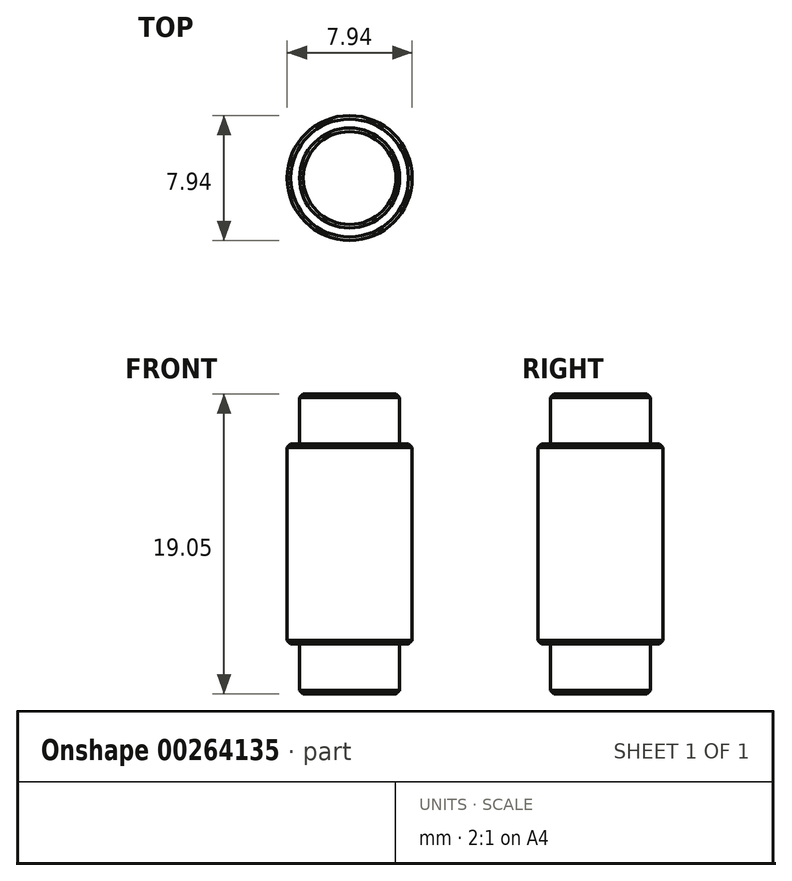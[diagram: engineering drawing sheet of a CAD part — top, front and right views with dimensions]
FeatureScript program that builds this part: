
annotation { "Feature Type Name" : "Feature", "Feature Type Description" : "" }
export const myFeature = defineFeature(function(context is Context, id is Id, definition is map)
    precondition{}
    {
        {
            var Q0;
            Q0=qCreatedBy(makeId("Top.planeOp"),FACE);
            var sketch = newSketch(context, id + "F0", { "sketchPlane" : qUnion([Q0])});
            skCircle(sketch, "E0", {"center": v(0, 0) * mm, "radius": 3.18 * mm});
            skSolve(sketch);
        }
        {
            var Q0;
            Q0 = qSketchRegion(id + "F0", true);
            extrude(context, id + "F1", {"entities" : qUnion([Q0]), "depth" : 3.17 * mm});
        }
        {
            var Q0;
            Q0=makeQuery(id+"F1.opExtrude","CAP_FACE",FACE,{"disambiguationData":[OSD([sQuery(id+"F0.wireOp",EDGE,"E0")])],"isStart":false});
            var sketch = newSketch(context, id + "F2", { "sketchPlane" : qUnion([Q0])});
            skCircle(sketch, "E1", {"center": v(0, 0) * mm, "radius": 3.97 * mm});
            skSolve(sketch);
        }
        {
            var Q0;
            Q0 = qSketchRegion(id + "F2", true);
            extrude(context, id + "F3", {"entities" : qUnion([Q0]), "operationType" : NewBodyOperationType.ADD, "depth" : 12.7 * mm});
        }
        {
            var Q0;
            Q0=makeQuery(id+"F3.opExtrude","CAP_FACE",FACE,{"disambiguationData":[OSD([sQuery(id+"F2.wireOp",EDGE,"E1")])],"isStart":false});
            var sketch = newSketch(context, id + "F4", { "sketchPlane" : qUnion([Q0])});
            skCircle(sketch, "E2", {"center": v(0, 0) * mm, "radius": 3.18 * mm});
            skSolve(sketch);
        }
        {
            var Q0;
            Q0 = qSketchRegion(id + "F4", true);
            extrude(context, id + "F5", {"entities" : qUnion([Q0]), "operationType" : NewBodyOperationType.ADD, "depth" : 3.17 * mm});
        }
        {
            var Q0;
            Q0=makeQuery(id+"F5.opExtrude","CAP_EDGE",EDGE,{"disambiguationData":[OSD([sQuery(id+"F4.wireOp",EDGE,"E2")])],"isStart":false});
            var Q1;
            Q1=makeQuery(id+"F3.opExtrude","CAP_EDGE",EDGE,{"disambiguationData":[OSD([sQuery(id+"F2.wireOp",EDGE,"E1")])],"isStart":false});
            var Q2;
            Q2=makeQuery(id+"F3.opExtrude","CAP_EDGE",EDGE,{"disambiguationData":[OSD([sQuery(id+"F2.wireOp",EDGE,"E1")])],"isStart":true});
            var Q3;
            Q3=makeQuery(id+"F1.opExtrude","CAP_EDGE",EDGE,{"disambiguationData":[OSD([sQuery(id+"F0.wireOp",EDGE,"E0")])],"isStart":true});
            chamfer(context, id + "F6", {"entities" : qUnion([Q0, Q1, Q2, Q3]), "width" : 0.23 * mm, "tangentPropagation" : true});
        }
    });
